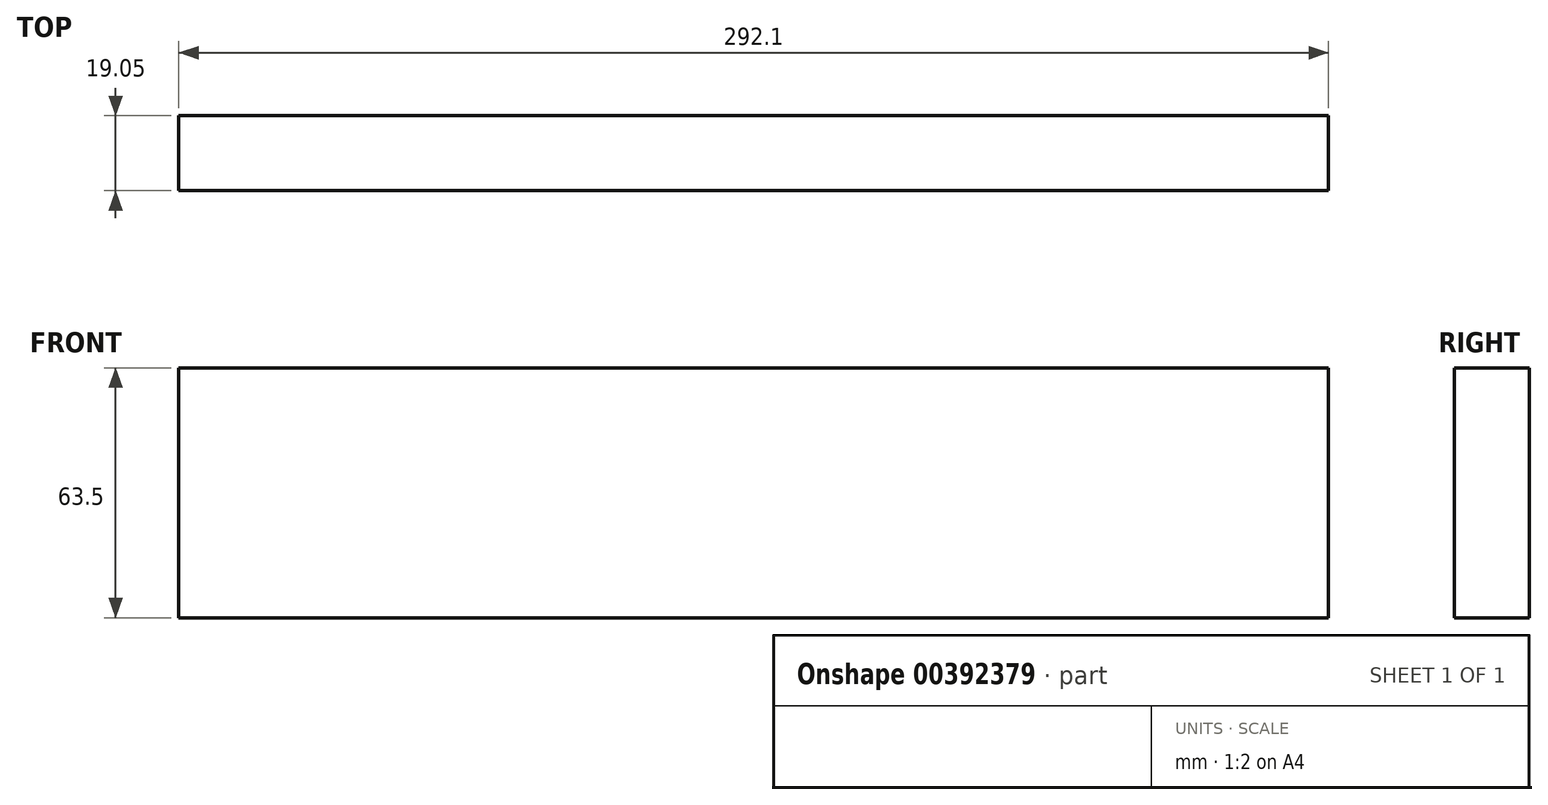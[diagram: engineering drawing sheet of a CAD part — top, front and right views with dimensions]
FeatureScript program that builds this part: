
annotation { "Feature Type Name" : "Feature", "Feature Type Description" : "" }
export const myFeature = defineFeature(function(context is Context, id is Id, definition is map)
    precondition{}
    {
        {
            var Q0;
            Q0=qCreatedBy(makeId("Front.planeOp"),FACE);
            var sketch = newSketch(context, id + "F0", { "sketchPlane" : qUnion([Q0])});
            skLineSegment(sketch, "E0.bottom", {"start": v(0, 0) * mm, "end": v(-292.1, 0) * mm});
            skLineSegment(sketch, "E0.top", {"start": v(0, 63.5) * mm, "end": v(-292.1, 63.5) * mm});
            skLineSegment(sketch, "E0.left", {"start": v(0, 0) * mm, "end": v(0, 63.5) * mm});
            skLineSegment(sketch, "E0.right", {"start": v(-292.1, 0) * mm, "end": v(-292.1, 63.5) * mm});
            skSolve(sketch);
        }
        {
            var Q0;
            Q0=makeQuery(id+"F0.imprint","IMPRINT",FACE,{"disambiguationData":[TD([[makeQuery(id+"F0.imprint","IMPRINT",EDGE,{"derivedFrom":sQuery(id+"F0.wireOp",EDGE,"E0.bottom")}),-1.0]])]});
            extrude(context, id + "F1", {"entities" : qUnion([Q0]), "depth" : 19.05 * mm});
        }
    });
